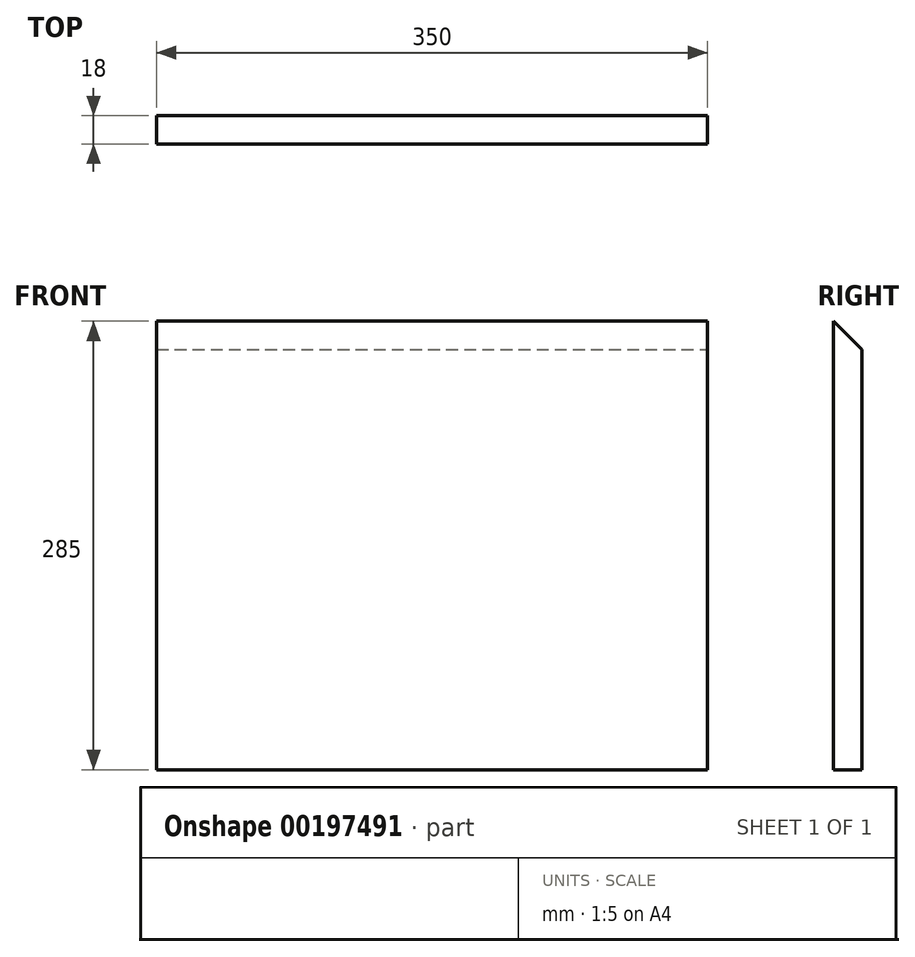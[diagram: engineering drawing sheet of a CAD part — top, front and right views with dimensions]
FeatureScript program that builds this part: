
annotation { "Feature Type Name" : "Feature", "Feature Type Description" : "" }
export const myFeature = defineFeature(function(context is Context, id is Id, definition is map)
    precondition{}
    {
        {
            var Q0;
            Q0=qCreatedBy(makeId("Front.planeOp"),FACE);
            var sketch = newSketch(context, id + "F0", { "sketchPlane" : qUnion([Q0])});
            skLineSegment(sketch, "E0.bottom", {"start": v(175, 142.5) * mm, "end": v(-175, 142.5) * mm});
            skLineSegment(sketch, "E0.top", {"start": v(175, -142.5) * mm, "end": v(-175, -142.5) * mm});
            skLineSegment(sketch, "E0.left", {"start": v(175, 142.5) * mm, "end": v(175, -142.5) * mm});
            skLineSegment(sketch, "E0.right", {"start": v(-175, 142.5) * mm, "end": v(-175, -142.5) * mm});
            skPoint(sketch, "E0.middle", {"position": v(0, 0) * mm});
            skSolve(sketch);
        }
        {
            var Q0;
            Q0 = qSketchRegion(id + "F0", true);
            extrude(context, id + "F1", {"entities" : qUnion([Q0]), "depth" : 18 * mm});
        }
        {
            var Q0;
            Q0=makeQuery(id+"F1.opExtrude","SWEPT_FACE",FACE,{"disambiguationData":[OSD([sQuery(id+"F0.wireOp",EDGE,"E0.left")])]});
            var sketch = newSketch(context, id + "F2", { "sketchPlane" : qUnion([Q0])});
            skLineSegment(sketch, "E1", {"start": v(-18, 142.5) * mm, "end": v(0, 142.5) * mm});
            skLineSegment(sketch, "E2", {"start": v(0, 142.5) * mm, "end": v(0, 124.5) * mm});
            skLineSegment(sketch, "E3", {"start": v(0, 124.5) * mm, "end": v(-18, 142.5) * mm});
            skSolve(sketch);
        }
        {
            var Q0;
            Q0 = qSketchRegion(id + "F2", true);
            extrude(context, id + "F3", {"entities" : qUnion([Q0]), "operationType" : NewBodyOperationType.REMOVE, "oppositeDirection" : true, "depth" : 370 * mm});
        }
    });
